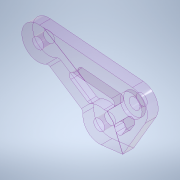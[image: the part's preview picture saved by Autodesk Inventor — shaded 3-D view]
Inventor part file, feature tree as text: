
AUTODESK INVENTOR PART (.ipt)
format: ipt  version: 2020.2 (Build 242310000, 310)  size: 492,032 bytes
history: native  units: mm
features: extrude x17, sketch x7, projected_geometry x6, other x2, hole x2
ambient origin geometry x8: Origin, YZ Plane, XZ Plane, XY Plane, X Axis, Y Axis, Z Axis, Center Point
bodies: Body1 (feature_tree)
feature tree (34):
  other  "ソリッド1"
  sketch  "スケッチ1"
  extrude  "押し出し1"  Depth=3.0mm TaperAngle=0.0deg
  extrude  "押し出し2"  Depth=0.05mm TaperAngle=0.0deg
  extrude  "押し出し3"  Depth=6.0mm
  sketch  "スケッチ3"
  extrude  "押し出し4"  Depth=1.0mm TaperAngle=0.0deg
  extrude  "押し出し5"  Depth=10.0mm TaperAngle=0.0deg
  hole  "穴1"  [1 undecoded]
  sketch  "スケッチ4"
  extrude  "押し出し6"  Depth=9.0mm
  extrude  "押し出し7"  Depth=9.0mm
  extrude  "押し出し8"  Depth=10.0mm TaperAngle=0.0deg
  extrude  "押し出し9"  Depth=3.0mm TaperAngle=0.0deg
  sketch  "スケッチ5"
  extrude  "押し出し10"  Depth=0.05mm TaperAngle=0.0deg
  extrude  "押し出し12"  Depth=0.05mm TaperAngle=0.0deg
  extrude  "押し出し13"  Depth=3.0mm TaperAngle=0.0deg
  extrude  "押し出し14"  Depth=0.05mm TaperAngle=0.0deg
  extrude  "押し出し11"  Depth=9.0mm
  hole  "穴2"  [1 undecoded]
  sketch  "スケッチ6"
  sketch  "スケッチ7"
  extrude  "押し出し15"  Depth=3.0mm TaperAngle=0.0deg
  extrude  "押し出し16"  Depth=10.0mm TaperAngle=0.0deg
  extrude  "押し出し17"  Depth=3.0mm TaperAngle=0.0deg
  sketch  "スケッチ2"
  projected_geometry  "投影ループ1"
  projected_geometry  "投影ループ2"
  projected_geometry  "投影ループ3"
  projected_geometry  "投影ループ4"
  projected_geometry  "投影ループ5"
  projected_geometry  "投影ループ6"
  other  "断面エッジを投影1"
note: 2 required parameter values undecoded (feature->parameter linkage not recoverable at this tier; creation-order binding heuristic only, values carry confidence <= 0.55)
